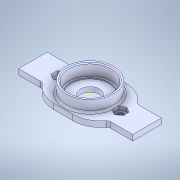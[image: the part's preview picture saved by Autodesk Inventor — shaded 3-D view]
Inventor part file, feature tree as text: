
AUTODESK INVENTOR PART (.ipt)
format: ipt  version: 2021 (Build 250183000, 183)  size: 241,152 bytes
history: mixed  units: in
note: dims shown in document units (in); Inventor stores cm internally (conversion verified against a paired STEP export)
features: sketch x8, extrude x6, fillet x2, delete_face x1, chamfer x1, other x1, imported_body x1
ambient origin geometry x8: Origin, YZ Plane, XZ Plane, XY Plane, X Axis, Y Axis, Z Axis, Center Point
bodies: Solid1 (imported_parasolid)
feature tree (20):
  extrude  "Extrusion1"  Depth=0.3937in TaperAngle=0.0deg
  extrude  "Extrusion2"  TaperAngle=0.0deg  [1 undecoded]
  sketch  "Sketch5"  dims[d8=0.9843in d9=0.3937in d10=0.0in]
  delete_face  "Delete Face1"
  extrude  "Extrusion4"  Depth=0.3937in TaperAngle=0.0deg
  extrude  "Extrusion5"  Depth=0.3937in TaperAngle=0.0deg
  chamfer  "Chamfer1"  Distance=0.0197in Angle=45.0deg
  sketch  "Sketch8"  dims[d34=2.3622in d35=0.5906in d36=0.3937in d37=0.0in]
  fillet  "Fillet1"  Radius=0.0394in
  extrude  "Extrusion8"  Depth=0.3937in TaperAngle=0.0deg
  extrude  "Extrusion9"  Depth=0.5906in
  fillet  "Fillet2"  Radius=0.3937in
  sketch  "Sketch1"  dims[d0=0.7874in d1=0.3937in d2=0.0in]
  sketch  "Sketch2"  dims[d3=0.3937in d4=0.0in d5=0.0in]
  sketch  "Sketch6"  dims[d11=0.878in d12=0.3937in d13=0.0in d14=0.0197in d15=0.0787in d16=45.0deg d20=0.0394in]
  sketch  "Sketch7"  dims[d31=0.1378in d32=0.3937in d33=0.0in]
  sketch  "Sketch13"  dims[d38=0.0787in]
  sketch  "Sketch14"
  other  "Cut-Extrude3"
  imported_body  NMx_Import_Brep_tag  [imported B-rep: ~33 faces, bbox_mm=[60.0, 3.0, 28.0]]
note: 1 required parameter value undecoded (feature->parameter linkage not recoverable at this tier; creation-order binding heuristic only, values carry confidence <= 0.55)
